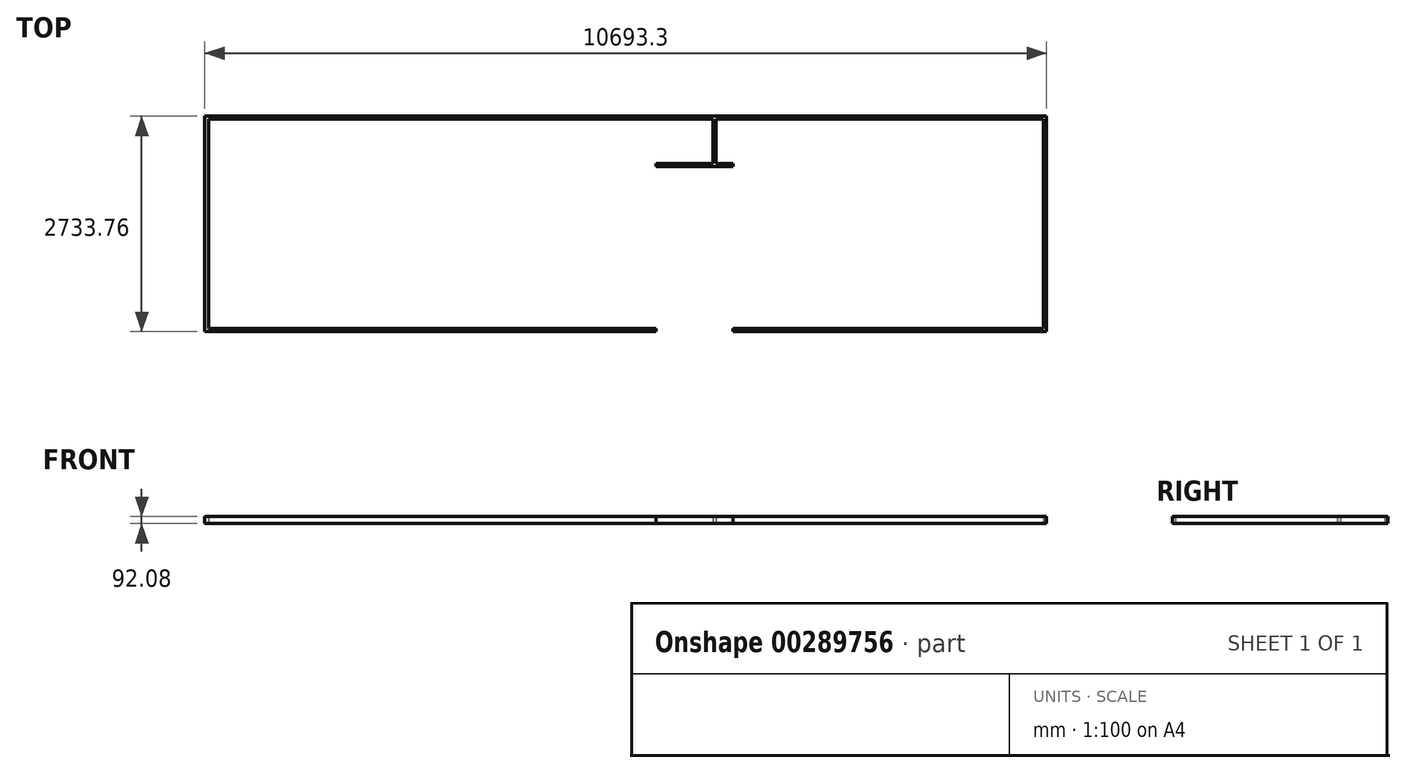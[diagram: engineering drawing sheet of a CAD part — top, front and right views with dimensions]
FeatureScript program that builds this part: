
annotation { "Feature Type Name" : "Feature", "Feature Type Description" : "" }
export const myFeature = defineFeature(function(context is Context, id is Id, definition is map)
    precondition{}
    {
        {
            var Q0;
            Q0=qCreatedBy(makeId("Top.planeOp"),FACE);
            var sketch = newSketch(context, id + "F0", { "sketchPlane" : qUnion([Q0])});
            skLineSegment(sketch, "E0.bottom", {"start": v(5346.65, -1366.88) * mm, "end": v(-5346.65, -1366.88) * mm});
            skLineSegment(sketch, "E0.top", {"start": v(5346.65, 1366.88) * mm, "end": v(-5346.65, 1366.88) * mm});
            skLineSegment(sketch, "E0.left", {"start": v(5346.65, -1366.88) * mm, "end": v(5346.65, 1366.88) * mm});
            skLineSegment(sketch, "E0.right", {"start": v(-5346.65, -1366.88) * mm, "end": v(-5346.65, 1366.88) * mm});
            skPoint(sketch, "E0.middle", {"position": v(0, 0) * mm});
            skLineSegment(sketch, "E1.bottom", {"start": v(-5300.93, 1328.78) * mm, "end": v(5308.55, 1328.78) * mm});
            skLineSegment(sketch, "E1.top", {"start": v(-5300.93, -1328.78) * mm, "end": v(5308.55, -1328.78) * mm});
            skLineSegment(sketch, "E1.left", {"start": v(-5300.93, 1328.78) * mm, "end": v(-5300.93, -1328.78) * mm});
            skLineSegment(sketch, "E1.right", {"start": v(5308.55, 1328.78) * mm, "end": v(5308.55, -1328.78) * mm});
            skLineSegment(sketch, "E2", {"start": v(0, -1328.78) * mm, "end": v(0, 1328.78) * mm, "construction": true});
            skLineSegment(sketch, "E3.bottom", {"start": v(387.25, 1328.78) * mm, "end": v(1365.15, 1328.78) * mm});
            skLineSegment(sketch, "E3.top", {"start": v(387.25, -1328.78) * mm, "end": v(1365.15, -1328.78) * mm});
            skLineSegment(sketch, "E3.left", {"start": v(387.25, 1328.78) * mm, "end": v(387.25, -1328.78) * mm});
            skLineSegment(sketch, "E3.right", {"start": v(1365.15, 1328.78) * mm, "end": v(1365.15, -1328.78) * mm});
            skLineSegment(sketch, "E4.bottom", {"start": v(387.25, 728.62) * mm, "end": v(1365.15, 728.62) * mm});
            skLineSegment(sketch, "E4.top", {"start": v(387.25, 766.72) * mm, "end": v(1365.15, 766.72) * mm});
            skLineSegment(sketch, "E4.left", {"start": v(387.25, 728.62) * mm, "end": v(387.25, 766.72) * mm});
            skLineSegment(sketch, "E4.right", {"start": v(1365.15, 728.62) * mm, "end": v(1365.15, 766.72) * mm});
            skLineSegment(sketch, "E5", {"start": v(349.15, 1328.78) * mm, "end": v(349.15, -1328.78) * mm});
            skLineSegment(sketch, "E6", {"start": v(1403.25, 1328.78) * mm, "end": v(1403.25, -1328.78) * mm});
            skLineSegment(sketch, "E7", {"start": v(876.2, 766.72) * mm, "end": v(876.2, 1328.78) * mm, "construction": true});
            skLineSegment(sketch, "E8.bottom", {"start": v(857, 1328.78) * mm, "end": v(895.4, 1328.78) * mm});
            skLineSegment(sketch, "E8.top", {"start": v(857, 766.72) * mm, "end": v(895.4, 766.72) * mm});
            skLineSegment(sketch, "E8.left", {"start": v(857, 1328.78) * mm, "end": v(857, 766.72) * mm});
            skLineSegment(sketch, "E8.right", {"start": v(895.4, 1328.78) * mm, "end": v(895.4, 766.72) * mm});
            skLineSegment(sketch, "E9.bottom", {"start": v(603.1, 1328.78) * mm, "end": v(641.2, 1328.78) * mm});
            skLineSegment(sketch, "E9.top", {"start": v(603.1, 766.72) * mm, "end": v(641.2, 766.72) * mm});
            skLineSegment(sketch, "E9.left", {"start": v(603.1, 1328.78) * mm, "end": v(603.1, 766.72) * mm});
            skLineSegment(sketch, "E9.right", {"start": v(641.2, 1328.78) * mm, "end": v(641.2, 766.72) * mm});
            skLineSegment(sketch, "E10", {"start": v(622.15, 1328.78) * mm, "end": v(622.15, 766.72) * mm, "construction": true});
            skLineSegment(sketch, "E11.MirrorCS", {"start": v(1111.2, 1328.78) * mm, "end": v(1111.2, 766.72) * mm});
            skLineSegment(sketch, "E12.MirrorCS", {"start": v(1149.3, 1328.78) * mm, "end": v(1149.3, 766.72) * mm});
            skLineSegment(sketch, "E13.bottom", {"start": v(4905.3, 1328.78) * mm, "end": v(4943.4, 1328.78) * mm});
            skLineSegment(sketch, "E13.top", {"start": v(4905.3, -1328.78) * mm, "end": v(4943.4, -1328.78) * mm});
            skLineSegment(sketch, "E13.left", {"start": v(4905.3, 1328.78) * mm, "end": v(4905.3, -1328.78) * mm});
            skLineSegment(sketch, "E13.right", {"start": v(4943.4, 1328.78) * mm, "end": v(4943.4, -1328.78) * mm});
            skLineSegment(sketch, "E14.bottom", {"start": v(4499, 1328.78) * mm, "end": v(4537.1, 1328.78) * mm});
            skLineSegment(sketch, "E14.top", {"start": v(4499, -1328.78) * mm, "end": v(4537.1, -1328.78) * mm});
            skLineSegment(sketch, "E14.left", {"start": v(4499, 1328.78) * mm, "end": v(4499, -1328.78) * mm});
            skLineSegment(sketch, "E14.right", {"start": v(4537.1, 1328.78) * mm, "end": v(4537.1, -1328.78) * mm});
            skLineSegment(sketch, "E15.bottom", {"start": v(4092.7, 1328.78) * mm, "end": v(4130.8, 1328.78) * mm});
            skLineSegment(sketch, "E15.top", {"start": v(4092.7, -1328.78) * mm, "end": v(4130.8, -1328.78) * mm});
            skLineSegment(sketch, "E15.left", {"start": v(4092.7, 1328.78) * mm, "end": v(4092.7, -1328.78) * mm});
            skLineSegment(sketch, "E15.right", {"start": v(4130.8, 1328.78) * mm, "end": v(4130.8, -1328.78) * mm});
            skLineSegment(sketch, "E16.bottom", {"start": v(3686.4, 1328.78) * mm, "end": v(3724.5, 1328.78) * mm});
            skLineSegment(sketch, "E16.top", {"start": v(3686.4, -1328.78) * mm, "end": v(3724.5, -1328.78) * mm});
            skLineSegment(sketch, "E16.left", {"start": v(3686.4, 1328.78) * mm, "end": v(3686.4, -1328.78) * mm});
            skLineSegment(sketch, "E16.right", {"start": v(3724.5, 1328.78) * mm, "end": v(3724.5, -1328.78) * mm});
            skLineSegment(sketch, "E17.bottom", {"start": v(3280.1, 1328.78) * mm, "end": v(3318.2, 1328.78) * mm});
            skLineSegment(sketch, "E17.top", {"start": v(3280.1, -1328.78) * mm, "end": v(3318.2, -1328.78) * mm});
            skLineSegment(sketch, "E17.left", {"start": v(3280.1, 1328.78) * mm, "end": v(3280.1, -1328.78) * mm});
            skLineSegment(sketch, "E17.right", {"start": v(3318.2, 1328.78) * mm, "end": v(3318.2, -1328.78) * mm});
            skLineSegment(sketch, "E18.bottom", {"start": v(2873.8, 1328.78) * mm, "end": v(2911.9, 1328.78) * mm});
            skLineSegment(sketch, "E18.top", {"start": v(2873.8, -1328.78) * mm, "end": v(2911.9, -1328.78) * mm});
            skLineSegment(sketch, "E18.left", {"start": v(2873.8, 1328.78) * mm, "end": v(2873.8, -1328.78) * mm});
            skLineSegment(sketch, "E18.right", {"start": v(2911.9, 1328.78) * mm, "end": v(2911.9, -1328.78) * mm});
            skLineSegment(sketch, "E19.bottom", {"start": v(2467.5, 1328.78) * mm, "end": v(2505.6, 1328.78) * mm});
            skLineSegment(sketch, "E19.top", {"start": v(2467.5, -1328.78) * mm, "end": v(2505.6, -1328.78) * mm});
            skLineSegment(sketch, "E19.left", {"start": v(2467.5, 1328.78) * mm, "end": v(2467.5, -1328.78) * mm});
            skLineSegment(sketch, "E19.right", {"start": v(2505.6, 1328.78) * mm, "end": v(2505.6, -1328.78) * mm});
            skLineSegment(sketch, "E20.bottom", {"start": v(2061.21, 1328.78) * mm, "end": v(2099.31, 1328.78) * mm});
            skLineSegment(sketch, "E20.top", {"start": v(2061.21, -1328.78) * mm, "end": v(2099.31, -1328.78) * mm});
            skLineSegment(sketch, "E20.left", {"start": v(2061.21, 1328.78) * mm, "end": v(2061.21, -1328.78) * mm});
            skLineSegment(sketch, "E20.right", {"start": v(2099.31, 1328.78) * mm, "end": v(2099.31, -1328.78) * mm});
            skLineSegment(sketch, "E21.bottom", {"start": v(1654.91, 1328.78) * mm, "end": v(1693.01, 1328.78) * mm});
            skLineSegment(sketch, "E21.top", {"start": v(1654.91, -1328.78) * mm, "end": v(1693.01, -1328.78) * mm});
            skLineSegment(sketch, "E21.left", {"start": v(1654.91, 1328.78) * mm, "end": v(1654.91, -1328.78) * mm});
            skLineSegment(sketch, "E21.right", {"start": v(1693.01, 1328.78) * mm, "end": v(1693.01, -1328.78) * mm});
            skLineSegment(sketch, "E22.bottom", {"start": v(-4932.73, 1328.78) * mm, "end": v(-4894.63, 1328.78) * mm});
            skLineSegment(sketch, "E22.top", {"start": v(-4932.73, -1328.78) * mm, "end": v(-4894.63, -1328.78) * mm});
            skLineSegment(sketch, "E22.left", {"start": v(-4932.73, 1328.78) * mm, "end": v(-4932.73, -1328.78) * mm});
            skLineSegment(sketch, "E22.right", {"start": v(-4894.63, 1328.78) * mm, "end": v(-4894.63, -1328.78) * mm});
            skLineSegment(sketch, "E23.bottom", {"start": v(-4526.43, 1328.78) * mm, "end": v(-4488.33, 1328.78) * mm});
            skLineSegment(sketch, "E23.top", {"start": v(-4526.43, -1328.78) * mm, "end": v(-4488.33, -1328.78) * mm});
            skLineSegment(sketch, "E23.left", {"start": v(-4526.43, 1328.78) * mm, "end": v(-4526.43, -1328.78) * mm});
            skLineSegment(sketch, "E23.right", {"start": v(-4488.33, 1328.78) * mm, "end": v(-4488.33, -1328.78) * mm});
            skLineSegment(sketch, "E24.bottom", {"start": v(-4120.13, 1328.78) * mm, "end": v(-4082.03, 1328.78) * mm});
            skLineSegment(sketch, "E24.top", {"start": v(-4120.13, -1328.78) * mm, "end": v(-4082.03, -1328.78) * mm});
            skLineSegment(sketch, "E24.left", {"start": v(-4120.13, 1328.78) * mm, "end": v(-4120.13, -1328.78) * mm});
            skLineSegment(sketch, "E24.right", {"start": v(-4082.03, 1328.78) * mm, "end": v(-4082.03, -1328.78) * mm});
            skLineSegment(sketch, "E25.bottom", {"start": v(-3713.84, 1328.78) * mm, "end": v(-3675.74, 1328.78) * mm});
            skLineSegment(sketch, "E25.top", {"start": v(-3713.84, -1328.78) * mm, "end": v(-3675.74, -1328.78) * mm});
            skLineSegment(sketch, "E25.left", {"start": v(-3713.84, 1328.78) * mm, "end": v(-3713.84, -1328.78) * mm});
            skLineSegment(sketch, "E25.right", {"start": v(-3675.74, 1328.78) * mm, "end": v(-3675.74, -1328.78) * mm});
            skLineSegment(sketch, "E26.bottom", {"start": v(-3307.54, 1328.78) * mm, "end": v(-3269.44, 1328.78) * mm});
            skLineSegment(sketch, "E26.top", {"start": v(-3307.54, -1328.78) * mm, "end": v(-3269.44, -1328.78) * mm});
            skLineSegment(sketch, "E26.left", {"start": v(-3307.54, 1328.78) * mm, "end": v(-3307.54, -1328.78) * mm});
            skLineSegment(sketch, "E26.right", {"start": v(-3269.44, 1328.78) * mm, "end": v(-3269.44, -1328.78) * mm});
            skLineSegment(sketch, "E27.bottom", {"start": v(-2901.24, 1328.78) * mm, "end": v(-2863.14, 1328.78) * mm});
            skLineSegment(sketch, "E27.top", {"start": v(-2901.24, -1328.78) * mm, "end": v(-2863.14, -1328.78) * mm});
            skLineSegment(sketch, "E27.left", {"start": v(-2901.24, 1328.78) * mm, "end": v(-2901.24, -1328.78) * mm});
            skLineSegment(sketch, "E27.right", {"start": v(-2863.14, 1328.78) * mm, "end": v(-2863.14, -1328.78) * mm});
            skLineSegment(sketch, "E28.bottom", {"start": v(-2494.94, 1328.78) * mm, "end": v(-2456.84, 1328.78) * mm});
            skLineSegment(sketch, "E28.top", {"start": v(-2494.94, -1328.78) * mm, "end": v(-2456.84, -1328.78) * mm});
            skLineSegment(sketch, "E28.left", {"start": v(-2494.94, 1328.78) * mm, "end": v(-2494.94, -1328.78) * mm});
            skLineSegment(sketch, "E28.right", {"start": v(-2456.84, 1328.78) * mm, "end": v(-2456.84, -1328.78) * mm});
            skLineSegment(sketch, "E29.bottom", {"start": v(-2088.64, 1328.78) * mm, "end": v(-2050.54, 1328.78) * mm});
            skLineSegment(sketch, "E29.top", {"start": v(-2088.64, -1328.78) * mm, "end": v(-2050.54, -1328.78) * mm});
            skLineSegment(sketch, "E29.left", {"start": v(-2088.64, 1328.78) * mm, "end": v(-2088.64, -1328.78) * mm});
            skLineSegment(sketch, "E29.right", {"start": v(-2050.54, 1328.78) * mm, "end": v(-2050.54, -1328.78) * mm});
            skLineSegment(sketch, "E30.bottom", {"start": v(-1682.34, 1328.78) * mm, "end": v(-1644.24, 1328.78) * mm});
            skLineSegment(sketch, "E30.top", {"start": v(-1682.34, -1328.78) * mm, "end": v(-1644.24, -1328.78) * mm});
            skLineSegment(sketch, "E30.left", {"start": v(-1682.34, 1328.78) * mm, "end": v(-1682.34, -1328.78) * mm});
            skLineSegment(sketch, "E30.right", {"start": v(-1644.24, 1328.78) * mm, "end": v(-1644.24, -1328.78) * mm});
            skLineSegment(sketch, "E31.bottom", {"start": v(-1276.05, 1328.78) * mm, "end": v(-1237.95, 1328.78) * mm});
            skLineSegment(sketch, "E31.top", {"start": v(-1276.05, -1328.78) * mm, "end": v(-1237.95, -1328.78) * mm});
            skLineSegment(sketch, "E31.left", {"start": v(-1276.05, 1328.78) * mm, "end": v(-1276.05, -1328.78) * mm});
            skLineSegment(sketch, "E31.right", {"start": v(-1237.95, 1328.78) * mm, "end": v(-1237.95, -1328.78) * mm});
            skLineSegment(sketch, "E32.bottom", {"start": v(-869.75, 1328.78) * mm, "end": v(-831.65, 1328.78) * mm});
            skLineSegment(sketch, "E32.top", {"start": v(-869.75, -1328.78) * mm, "end": v(-831.65, -1328.78) * mm});
            skLineSegment(sketch, "E32.left", {"start": v(-869.75, 1328.78) * mm, "end": v(-869.75, -1328.78) * mm});
            skLineSegment(sketch, "E32.right", {"start": v(-831.65, 1328.78) * mm, "end": v(-831.65, -1328.78) * mm});
            skLineSegment(sketch, "E33.bottom", {"start": v(-463.45, 1328.78) * mm, "end": v(-425.35, 1328.78) * mm});
            skLineSegment(sketch, "E33.top", {"start": v(-463.45, -1328.78) * mm, "end": v(-425.35, -1328.78) * mm});
            skLineSegment(sketch, "E33.left", {"start": v(-463.45, 1328.78) * mm, "end": v(-463.45, -1328.78) * mm});
            skLineSegment(sketch, "E33.right", {"start": v(-425.35, 1328.78) * mm, "end": v(-425.35, -1328.78) * mm});
            skLineSegment(sketch, "E34.bottom", {"start": v(-57.15, 1328.78) * mm, "end": v(-19.05, 1328.78) * mm});
            skLineSegment(sketch, "E34.top", {"start": v(-57.15, -1328.78) * mm, "end": v(-19.05, -1328.78) * mm});
            skLineSegment(sketch, "E34.left", {"start": v(-57.15, 1328.78) * mm, "end": v(-57.15, -1328.78) * mm});
            skLineSegment(sketch, "E34.right", {"start": v(-19.05, 1328.78) * mm, "end": v(-19.05, -1328.78) * mm});
            skLineSegment(sketch, "E35", {"start": v(1365.15, -1328.78) * mm, "end": v(1365.15, -1366.88) * mm});
            skLineSegment(sketch, "E36", {"start": v(387.25, -1328.78) * mm, "end": v(387.25, -1366.88) * mm});
            skSolve(sketch);
        }
        {
            var Q0;
            {var subQ0=sQuery(id+"F0.wireOp",EDGE,"e03bbd14-4e46-43d8-a5f9-80b2dea7db7f0.MirrorCS");Q0=makeQuery(id+"F0.imprint","IMPRINT",FACE,{"disambiguationData":[TD([[makeQuery(id+"F0.imprint","IMPRINT",EDGE,{"derivedFrom":subQ0}),1.0]])]});}
            var Q1;
            {var subQ7=sQuery(id+"F0.wireOp",EDGE,"EFqx7HEP-Nfe9-0ldO-Yoev-NmYAcbnf758y");Q1=makeQuery(id+"F0.imprint","IMPRINT",FACE,{"disambiguationData":[TD([[makeQuery(id+"F0.imprint","IMPRINT",EDGE,{"derivedFrom":subQ7}),-1.0]])]});}
            var Q2;
            {var subQ0=sQuery(id+"F0.wireOp",EDGE,"edbdd21b-7951-4497-ac7e-6e46abb4ccd70.MirrorCS");Q2=makeQuery(id+"F0.imprint","IMPRINT",FACE,{"disambiguationData":[TD([[makeQuery(id+"F0.imprint","IMPRINT",EDGE,{"derivedFrom":subQ0}),-1.0]])]});}
            var Q3;
            {var subQ0=sQuery(id+"F0.wireOp",EDGE,"7de17b8e-8469-475a-b975-fd82b060c23f0.MirrorCS");Q3=makeQuery(id+"F0.imprint","IMPRINT",FACE,{"disambiguationData":[TD([[makeQuery(id+"F0.imprint","IMPRINT",EDGE,{"derivedFrom":subQ0}),1.0]])]});}
            var Q4;
            {var subQ5=sQuery(id+"F0.wireOp",EDGE,"4AthFqkJ-wqFj-7w0H-RTdV-ZVLi3eRejgEJ.bottom");var subQ8=sQuery(id+"F0.wireOp",EDGE,"8f4d6e74-220d-450d-a5c4-15dd5d45fac50.MirrorCS");var subQ10=makeQuery(id+"F0.imprint","INTERSECT",VERTEX,{"derivedFrom":[subQ5,subQ8]});Q4=makeQuery(id+"F0.imprint","IMPRINT",FACE,{"disambiguationData":[TD([[makeQuery(id+"F0.imprint","IMPRINT",EDGE,{"disambiguationData":[TD([[subQ10,-1.0]])],"derivedFrom":subQ5}),1.0]])]});}
            var Q5;
            {var subQ0=sQuery(id+"F0.wireOp",EDGE,"b7a96eb8-1ea0-4e2f-8a00-b5aa0dec934b0.MirrorCS");Q5=makeQuery(id+"F0.imprint","IMPRINT",FACE,{"disambiguationData":[TD([[makeQuery(id+"F0.imprint","IMPRINT",EDGE,{"derivedFrom":subQ0}),-1.0]])]});}
            var Q6;
            {var subQ0=sQuery(id+"F0.wireOp",EDGE,"da11186a-d0f2-4cc5-8c91-6d18c19f1f220.MirrorCS");Q6=makeQuery(id+"F0.imprint","IMPRINT",FACE,{"disambiguationData":[TD([[makeQuery(id+"F0.imprint","IMPRINT",EDGE,{"derivedFrom":subQ0}),-1.0]])]});}
            var Q7;
            {var subQ0=sQuery(id+"F0.wireOp",EDGE,"f72f8c2a-f3f3-459a-8ec0-e048655b896d0.MirrorCS");var subQ1=sQuery(id+"F0.wireOp",EDGE,"4AthFqkJ-wqFj-7w0H-RTdV-ZVLi3eRejgEJ.top");var subQ2=makeQuery(id+"F0.imprint","INTERSECT",VERTEX,{"derivedFrom":[subQ1,subQ0]});Q7=makeQuery(id+"F0.imprint","IMPRINT",FACE,{"disambiguationData":[TD([[makeQuery(id+"F0.imprint","IMPRINT",EDGE,{"disambiguationData":[TD([[subQ2,-1.0]])],"derivedFrom":subQ1}),1.0]])]});}
            var Q8;
            {var subQ5=sQuery(id+"F0.wireOp",EDGE,"eca8af08-4f88-4f9e-b7fb-055b73c8b4f30.MirrorCS");var subQ7=sQuery(id+"F0.wireOp",EDGE,"4AthFqkJ-wqFj-7w0H-RTdV-ZVLi3eRejgEJ.bottom");var subQ8=makeQuery(id+"F0.imprint","INTERSECT",VERTEX,{"derivedFrom":[subQ7,subQ5]});Q8=makeQuery(id+"F0.imprint","IMPRINT",FACE,{"disambiguationData":[TD([[makeQuery(id+"F0.imprint","IMPRINT",EDGE,{"disambiguationData":[TD([[subQ8,-1.0]])],"derivedFrom":subQ7}),1.0]])]});}
            var Q9;
            {var subQ4=sQuery(id+"F0.wireOp",EDGE,"6c1e8db1-4096-4c37-9079-9901a149bb3d0.MirrorCS");var subQ7=sQuery(id+"F0.wireOp",EDGE,"4AthFqkJ-wqFj-7w0H-RTdV-ZVLi3eRejgEJ.bottom");var subQ10=makeQuery(id+"F0.imprint","INTERSECT",VERTEX,{"derivedFrom":[subQ7,subQ4]});Q9=makeQuery(id+"F0.imprint","IMPRINT",FACE,{"disambiguationData":[TD([[makeQuery(id+"F0.imprint","IMPRINT",EDGE,{"disambiguationData":[TD([[subQ10,-1.0]])],"derivedFrom":subQ7}),1.0]])]});}
            var Q10;
            {var subQ0=sQuery(id+"F0.wireOp",EDGE,"55050aa2-543b-4654-a200-01c89433912e0.MirrorCS");var subQ1=sQuery(id+"F0.wireOp",EDGE,"4AthFqkJ-wqFj-7w0H-RTdV-ZVLi3eRejgEJ.top");var subQ2=makeQuery(id+"F0.imprint","INTERSECT",VERTEX,{"derivedFrom":[subQ1,subQ0]});Q10=makeQuery(id+"F0.imprint","IMPRINT",FACE,{"disambiguationData":[TD([[makeQuery(id+"F0.imprint","IMPRINT",EDGE,{"disambiguationData":[TD([[subQ2,1.0]])],"derivedFrom":subQ1}),1.0]])]});}
            var Q11;
            {var subQ3=sQuery(id+"F0.wireOp",EDGE,"3aWXcNN2-d2y1-1F6M-5Hkd-EHZ6NJIHuSP8");Q11=makeQuery(id+"F0.imprint","IMPRINT",FACE,{"disambiguationData":[TD([[makeQuery(id+"F0.imprint","IMPRINT",EDGE,{"derivedFrom":subQ3}),-1.0]])]});}
            var Q12;
            {var subQ6=sQuery(id+"F0.wireOp",EDGE,"4AthFqkJ-wqFj-7w0H-RTdV-ZVLi3eRejgEJ.left");Q12=makeQuery(id+"F0.imprint","IMPRINT",FACE,{"disambiguationData":[TD([[makeQuery(id+"F0.imprint","IMPRINT",EDGE,{"derivedFrom":subQ6}),-1.0]])]});}
            var Q13;
            {var subQ0=sQuery(id+"F0.wireOp",EDGE,"92030646-e98a-4083-b465-eda06a02aa580.MirrorCS");Q13=makeQuery(id+"F0.imprint","IMPRINT",FACE,{"disambiguationData":[TD([[makeQuery(id+"F0.imprint","IMPRINT",EDGE,{"derivedFrom":subQ0}),1.0]])]});}
            var Q14;
            {var subQ0=sQuery(id+"F0.wireOp",EDGE,"0e344b7f-dcc7-4a3f-8939-196222c3ee7a0.MirrorCS");Q14=makeQuery(id+"F0.imprint","IMPRINT",FACE,{"disambiguationData":[TD([[makeQuery(id+"F0.imprint","IMPRINT",EDGE,{"derivedFrom":subQ0}),-1.0]])]});}
            var Q15;
            {var subQ0=sQuery(id+"F0.wireOp",EDGE,"95ca570f-170f-43a6-b84c-d3a65055c82b0.MirrorCS");Q15=makeQuery(id+"F0.imprint","IMPRINT",FACE,{"disambiguationData":[TD([[makeQuery(id+"F0.imprint","IMPRINT",EDGE,{"derivedFrom":subQ0}),1.0]])]});}
            var Q16;
            {var subQ4=sQuery(id+"F0.wireOp",EDGE,"8a681850-bd4a-4ca6-8d45-30870cc5114b0.MirrorCS");var subQ5=sQuery(id+"F0.wireOp",EDGE,"4AthFqkJ-wqFj-7w0H-RTdV-ZVLi3eRejgEJ.bottom");var subQ6=makeQuery(id+"F0.imprint","INTERSECT",VERTEX,{"derivedFrom":[subQ5,subQ4]});Q16=makeQuery(id+"F0.imprint","IMPRINT",FACE,{"disambiguationData":[TD([[makeQuery(id+"F0.imprint","IMPRINT",EDGE,{"disambiguationData":[TD([[subQ6,-1.0]])],"derivedFrom":subQ5}),1.0]])]});}
            var Q17;
            {var subQ4=sQuery(id+"F0.wireOp",EDGE,"4AthFqkJ-wqFj-7w0H-RTdV-ZVLi3eRejgEJ.bottom");var subQ8=sQuery(id+"F0.wireOp",EDGE,"5ed274ad-43b9-4acb-bec6-48bd2bb972420.MirrorCS");var subQ10=makeQuery(id+"F0.imprint","INTERSECT",VERTEX,{"derivedFrom":[subQ4,subQ8]});Q17=makeQuery(id+"F0.imprint","IMPRINT",FACE,{"disambiguationData":[TD([[makeQuery(id+"F0.imprint","IMPRINT",EDGE,{"disambiguationData":[TD([[subQ10,-1.0]])],"derivedFrom":subQ4}),1.0]])]});}
            var Q18;
            {var subQ5=sQuery(id+"F0.wireOp",EDGE,"bf3aad54-d5d8-4dbd-ba34-4691da0b365d0.MirrorCS");var subQ7=sQuery(id+"F0.wireOp",EDGE,"4AthFqkJ-wqFj-7w0H-RTdV-ZVLi3eRejgEJ.bottom");var subQ8=makeQuery(id+"F0.imprint","INTERSECT",VERTEX,{"derivedFrom":[subQ7,subQ5]});Q18=makeQuery(id+"F0.imprint","IMPRINT",FACE,{"disambiguationData":[TD([[makeQuery(id+"F0.imprint","IMPRINT",EDGE,{"disambiguationData":[TD([[subQ8,-1.0]])],"derivedFrom":subQ7}),1.0]])]});}
            var Q19;
            {var subQ0=sQuery(id+"F0.wireOp",EDGE,"7ad01133-0a83-40c2-aee9-f517a01396690.MirrorCS");var subQ1=sQuery(id+"F0.wireOp",EDGE,"4AthFqkJ-wqFj-7w0H-RTdV-ZVLi3eRejgEJ.top");var subQ2=makeQuery(id+"F0.imprint","INTERSECT",VERTEX,{"derivedFrom":[subQ1,subQ0]});Q19=makeQuery(id+"F0.imprint","IMPRINT",FACE,{"disambiguationData":[TD([[makeQuery(id+"F0.imprint","IMPRINT",EDGE,{"disambiguationData":[TD([[subQ2,1.0]])],"derivedFrom":subQ1}),1.0]])]});}
            var Q20;
            {var subQ3=sQuery(id+"F0.wireOp",EDGE,"0632b321-56e7-4b31-9cd1-585e07a893ff0.MirrorCS");var subQ4=sQuery(id+"F0.wireOp",EDGE,"4AthFqkJ-wqFj-7w0H-RTdV-ZVLi3eRejgEJ.bottom");var subQ5=makeQuery(id+"F0.imprint","INTERSECT",VERTEX,{"derivedFrom":[subQ4,subQ3]});Q20=makeQuery(id+"F0.imprint","IMPRINT",FACE,{"disambiguationData":[TD([[makeQuery(id+"F0.imprint","IMPRINT",EDGE,{"disambiguationData":[TD([[subQ5,-1.0]])],"derivedFrom":subQ4}),1.0]])]});}
            var Q21;
            {var subQ4=sQuery(id+"F0.wireOp",EDGE,"4AthFqkJ-wqFj-7w0H-RTdV-ZVLi3eRejgEJ.bottom");var subQ8=sQuery(id+"F0.wireOp",EDGE,"1bcce820-757c-45ce-a4fe-54bff22ba8310.MirrorCS");var subQ10=makeQuery(id+"F0.imprint","INTERSECT",VERTEX,{"derivedFrom":[subQ4,subQ8]});Q21=makeQuery(id+"F0.imprint","IMPRINT",FACE,{"disambiguationData":[TD([[makeQuery(id+"F0.imprint","IMPRINT",EDGE,{"disambiguationData":[TD([[subQ10,-1.0]])],"derivedFrom":subQ4}),1.0]])]});}
            var Q22;
            {var subQ8=sQuery(id+"F0.wireOp",EDGE,"4AthFqkJ-wqFj-7w0H-RTdV-ZVLi3eRejgEJ.right");Q22=makeQuery(id+"F0.imprint","IMPRINT",FACE,{"disambiguationData":[TD([[makeQuery(id+"F0.imprint","IMPRINT",EDGE,{"derivedFrom":subQ8}),1.0]])]});}
            var Q23;
            {var subQ0=sQuery(id+"F0.wireOp",EDGE,"1b9fc814-7275-47f6-8dd0-aeae657b9ac90.MirrorCS");var subQ1=sQuery(id+"F0.wireOp",EDGE,"4AthFqkJ-wqFj-7w0H-RTdV-ZVLi3eRejgEJ.top");var subQ2=makeQuery(id+"F0.imprint","INTERSECT",VERTEX,{"derivedFrom":[subQ1,subQ0]});Q23=makeQuery(id+"F0.imprint","IMPRINT",FACE,{"disambiguationData":[TD([[makeQuery(id+"F0.imprint","IMPRINT",EDGE,{"disambiguationData":[TD([[subQ2,-1.0]])],"derivedFrom":subQ1}),1.0]])]});}
            var Q24;
            {var subQ0=sQuery(id+"F0.wireOp",EDGE,"0493b29f-ec4a-4c4c-ac9e-8fdb3be76d310.MirrorCS");Q24=makeQuery(id+"F0.imprint","IMPRINT",FACE,{"disambiguationData":[TD([[makeQuery(id+"F0.imprint","IMPRINT",EDGE,{"derivedFrom":subQ0}),1.0]])]});}
            var Q25;
            {var subQ0=sQuery(id+"F0.wireOp",EDGE,"63c733ed-a5aa-43e7-ab23-9ab8c604324c0.MirrorCS");Q25=makeQuery(id+"F0.imprint","IMPRINT",FACE,{"disambiguationData":[TD([[makeQuery(id+"F0.imprint","IMPRINT",EDGE,{"derivedFrom":subQ0}),1.0]])]});}
            var Q26;
            {var subQ5=sQuery(id+"F0.wireOp",EDGE,"E6GgMG58-NzDt-iqJW-TLqZ-AtfXyUXh4wKe");Q26=makeQuery(id+"F0.imprint","IMPRINT",FACE,{"disambiguationData":[TD([[makeQuery(id+"F0.imprint","IMPRINT",EDGE,{"derivedFrom":subQ5}),1.0]])]});}
            var Q27;
            {var subQ6=sQuery(id+"F0.wireOp",EDGE,"3aWXcNN2-d2y1-1F6M-5Hkd-EHZ6NJIHuSP8");Q27=makeQuery(id+"F0.imprint","IMPRINT",FACE,{"disambiguationData":[TD([[makeQuery(id+"F0.imprint","IMPRINT",EDGE,{"derivedFrom":subQ6}),1.0]])]});}
            var Q28;
            {var subQ6=sQuery(id+"F0.wireOp",EDGE,"E6GgMG58-NzDt-iqJW-TLqZ-AtfXyUXh4wKe");Q28=makeQuery(id+"F0.imprint","IMPRINT",FACE,{"disambiguationData":[TD([[makeQuery(id+"F0.imprint","IMPRINT",EDGE,{"derivedFrom":subQ6}),-1.0]])]});}
            var Q29;
            {var subQ0=sQuery(id+"F0.wireOp",EDGE,"xTM1oSQN-q9p7-LrQJ-wgkP-syFjsQtJfwuK.bottom");Q29=makeQuery(id+"F0.imprint","IMPRINT",FACE,{"disambiguationData":[TD([[makeQuery(id+"F0.imprint","IMPRINT",EDGE,{"derivedFrom":subQ0}),-1.0]])]});}
            var Q30;
            {var subQ0=sQuery(id+"F0.wireOp",EDGE,"xTM1oSQN-q9p7-LrQJ-wgkP-syFjsQtJfwuK.top");Q30=makeQuery(id+"F0.imprint","IMPRINT",FACE,{"disambiguationData":[TD([[makeQuery(id+"F0.imprint","IMPRINT",EDGE,{"derivedFrom":subQ0}),1.0]])]});}
            var Q31;
            {var subQ1=sQuery(id+"F0.wireOp",EDGE,"xTM1oSQN-q9p7-LrQJ-wgkP-syFjsQtJfwuK.bottom");Q31=makeQuery(id+"F0.imprint","IMPRINT",FACE,{"disambiguationData":[TD([[makeQuery(id+"F0.imprint","IMPRINT",EDGE,{"derivedFrom":subQ1}),1.0]])]});}
            var Q32;
            Q32=makeQuery(id+"F0.imprint","IMPRINT",FACE,{"disambiguationData":[TD([[makeQuery(id+"F0.imprint","IMPRINT",EDGE,{"derivedFrom":sQuery(id+"F0.wireOp",EDGE,"w7in2STq-dmfq-Ztst-uc13-PS53EKAe34f7.top")}),1.0]])]});
            var Q33;
            {var subQ5=sQuery(id+"F0.wireOp",EDGE,"8ijx6biu-ALKk-pq3C-dhgc-nGGqiL4vIiWN");var subQ7=sQuery(id+"F0.wireOp",EDGE,"8a681850-bd4a-4ca6-8d45-30870cc5114b0.MirrorCS");var subQ8=makeQuery(id+"F0.imprint","INTERSECT",VERTEX,{"derivedFrom":[subQ7,subQ5]});Q33=makeQuery(id+"F0.imprint","IMPRINT",FACE,{"disambiguationData":[TD([[makeQuery(id+"F0.imprint","IMPRINT",EDGE,{"disambiguationData":[TD([[subQ8,1.0]])],"derivedFrom":subQ7}),-1.0]])]});}
            var Q34;
            {var subQ7=sQuery(id+"F0.wireOp",EDGE,"0632b321-56e7-4b31-9cd1-585e07a893ff0.MirrorCS");var subQ9=sQuery(id+"F0.wireOp",EDGE,"8ijx6biu-ALKk-pq3C-dhgc-nGGqiL4vIiWN");var subQ10=makeQuery(id+"F0.imprint","INTERSECT",VERTEX,{"derivedFrom":[subQ7,subQ9]});Q34=makeQuery(id+"F0.imprint","IMPRINT",FACE,{"disambiguationData":[TD([[makeQuery(id+"F0.imprint","IMPRINT",EDGE,{"disambiguationData":[TD([[subQ10,1.0]])],"derivedFrom":subQ7}),-1.0]])]});}
            var Q35;
            {var subQ5=sQuery(id+"F0.wireOp",EDGE,"8ijx6biu-ALKk-pq3C-dhgc-nGGqiL4vIiWN");var subQ6=sQuery(id+"F0.wireOp",EDGE,"019fe33c-2ba7-4981-a1aa-b8912489248e0.MirrorCS");var subQ7=makeQuery(id+"F0.imprint","INTERSECT",VERTEX,{"derivedFrom":[subQ6,subQ5]});Q35=makeQuery(id+"F0.imprint","IMPRINT",FACE,{"disambiguationData":[TD([[makeQuery(id+"F0.imprint","IMPRINT",EDGE,{"disambiguationData":[TD([[subQ7,1.0]])],"derivedFrom":subQ6}),-1.0]])]});}
            var Q36;
            {var subQ4=sQuery(id+"F0.wireOp",EDGE,"8ijx6biu-ALKk-pq3C-dhgc-nGGqiL4vIiWN");var subQ7=sQuery(id+"F0.wireOp",EDGE,"f7381abf-e9df-4e1a-a30e-4fe6b1d368c50.MirrorCS");var subQ8=makeQuery(id+"F0.imprint","INTERSECT",VERTEX,{"derivedFrom":[subQ7,subQ4]});Q36=makeQuery(id+"F0.imprint","IMPRINT",FACE,{"disambiguationData":[TD([[makeQuery(id+"F0.imprint","IMPRINT",EDGE,{"disambiguationData":[TD([[subQ8,1.0]])],"derivedFrom":subQ7}),-1.0]])]});}
            var Q37;
            {var subQ3=sQuery(id+"F0.wireOp",EDGE,"8ijx6biu-ALKk-pq3C-dhgc-nGGqiL4vIiWN");var subQ7=sQuery(id+"F0.wireOp",EDGE,"6c1e8db1-4096-4c37-9079-9901a149bb3d0.MirrorCS");var subQ8=makeQuery(id+"F0.imprint","INTERSECT",VERTEX,{"derivedFrom":[subQ7,subQ3]});Q37=makeQuery(id+"F0.imprint","IMPRINT",FACE,{"disambiguationData":[TD([[makeQuery(id+"F0.imprint","IMPRINT",EDGE,{"disambiguationData":[TD([[subQ8,1.0]])],"derivedFrom":subQ7}),-1.0]])]});}
            var Q38;
            {var subQ4=sQuery(id+"F0.wireOp",EDGE,"8ijx6biu-ALKk-pq3C-dhgc-nGGqiL4vIiWN");var subQ7=sQuery(id+"F0.wireOp",EDGE,"8f4d6e74-220d-450d-a5c4-15dd5d45fac50.MirrorCS");var subQ8=makeQuery(id+"F0.imprint","INTERSECT",VERTEX,{"derivedFrom":[subQ7,subQ4]});Q38=makeQuery(id+"F0.imprint","IMPRINT",FACE,{"disambiguationData":[TD([[makeQuery(id+"F0.imprint","IMPRINT",EDGE,{"disambiguationData":[TD([[subQ8,1.0]])],"derivedFrom":subQ7}),-1.0]])]});}
            var Q39;
            {var subQ0=sQuery(id+"F0.wireOp",EDGE,"KcFaNi3p-Mqzx-hNtU-70nu-rjvwtTVn4XIA");Q39=makeQuery(id+"F0.imprint","IMPRINT",FACE,{"disambiguationData":[TD([[makeQuery(id+"F0.imprint","IMPRINT",EDGE,{"derivedFrom":subQ0}),-1.0]])]});}
            var Q40;
            {var subQ7=sQuery(id+"F0.wireOp",EDGE,"JvJ4ZzyL-X5yR-yT1t-gWen-LnuBgDK7jZsF");Q40=makeQuery(id+"F0.imprint","IMPRINT",FACE,{"disambiguationData":[TD([[makeQuery(id+"F0.imprint","IMPRINT",EDGE,{"derivedFrom":subQ7}),1.0]])]});}
            var Q41;
            {var subQ5=sQuery(id+"F0.wireOp",EDGE,"8ijx6biu-ALKk-pq3C-dhgc-nGGqiL4vIiWN");var subQ6=sQuery(id+"F0.wireOp",EDGE,"bf3aad54-d5d8-4dbd-ba34-4691da0b365d0.MirrorCS");var subQ7=makeQuery(id+"F0.imprint","INTERSECT",VERTEX,{"derivedFrom":[subQ6,subQ5]});Q41=makeQuery(id+"F0.imprint","IMPRINT",FACE,{"disambiguationData":[TD([[makeQuery(id+"F0.imprint","IMPRINT",EDGE,{"disambiguationData":[TD([[subQ7,1.0]])],"derivedFrom":subQ6}),-1.0]])]});}
            var Q42;
            {var subQ5=sQuery(id+"F0.wireOp",EDGE,"8ijx6biu-ALKk-pq3C-dhgc-nGGqiL4vIiWN");var subQ7=sQuery(id+"F0.wireOp",EDGE,"5ed274ad-43b9-4acb-bec6-48bd2bb972420.MirrorCS");var subQ8=makeQuery(id+"F0.imprint","INTERSECT",VERTEX,{"derivedFrom":[subQ7,subQ5]});Q42=makeQuery(id+"F0.imprint","IMPRINT",FACE,{"disambiguationData":[TD([[makeQuery(id+"F0.imprint","IMPRINT",EDGE,{"disambiguationData":[TD([[subQ8,1.0]])],"derivedFrom":subQ7}),-1.0]])]});}
            var Q43;
            {var subQ0=sQuery(id+"F0.wireOp",EDGE,"EFqx7HEP-Nfe9-0ldO-Yoev-NmYAcbnf758y");Q43=makeQuery(id+"F0.imprint","IMPRINT",FACE,{"disambiguationData":[TD([[makeQuery(id+"F0.imprint","IMPRINT",EDGE,{"derivedFrom":subQ0}),1.0]])]});}
            var Q44;
            {var subQ0=sQuery(id+"F0.wireOp",EDGE,"QlbIkJlA-GZXo-uyBw-HzbM-woG2F7svoY3c");Q44=makeQuery(id+"F0.imprint","IMPRINT",FACE,{"disambiguationData":[TD([[makeQuery(id+"F0.imprint","IMPRINT",EDGE,{"derivedFrom":subQ0}),1.0]])]});}
            var Q45;
            {var subQ0=sQuery(id+"F0.wireOp",EDGE,"iGA4u3sP-0zRX-MU7R-LLKM-kgWDpWtacOll");Q45=makeQuery(id+"F0.imprint","IMPRINT",FACE,{"disambiguationData":[TD([[makeQuery(id+"F0.imprint","IMPRINT",EDGE,{"derivedFrom":subQ0}),-1.0]])]});}
            var Q46;
            {var subQ0=sQuery(id+"F0.wireOp",EDGE,"iGA4u3sP-0zRX-MU7R-LLKM-kgWDpWtacOll");Q46=makeQuery(id+"F0.imprint","IMPRINT",FACE,{"disambiguationData":[TD([[makeQuery(id+"F0.imprint","IMPRINT",EDGE,{"derivedFrom":subQ0}),1.0]])]});}
            var Q47;
            {var subQ0=sQuery(id+"F0.wireOp",EDGE,"t5sFcsg7-FEeG-W394-4G1u-bvZyn1PHE7l8");Q47=makeQuery(id+"F0.imprint","IMPRINT",FACE,{"disambiguationData":[TD([[makeQuery(id+"F0.imprint","IMPRINT",EDGE,{"derivedFrom":subQ0}),-1.0]])]});}
            var Q48;
            {var subQ0=sQuery(id+"F0.wireOp",EDGE,"gSGAxQI9-OKXq-k85j-osUc-OuGH0ZGV6Hf7");var subQ1=sQuery(id+"F0.wireOp",EDGE,"c3f41723-229c-4d74-ac07-4786d7f9cf2e0.MirrorCS");var subQ2=makeQuery(id+"F0.imprint","INTERSECT",VERTEX,{"derivedFrom":[subQ1,subQ0]});Q48=makeQuery(id+"F0.imprint","IMPRINT",FACE,{"disambiguationData":[TD([[makeQuery(id+"F0.imprint","IMPRINT",EDGE,{"disambiguationData":[TD([[subQ2,-1.0]])],"derivedFrom":subQ1}),1.0]])]});}
            var Q49;
            {var subQ0=sQuery(id+"F0.wireOp",EDGE,"gSGAxQI9-OKXq-k85j-osUc-OuGH0ZGV6Hf7");var subQ1=sQuery(id+"F0.wireOp",EDGE,"c3f41723-229c-4d74-ac07-4786d7f9cf2e0.MirrorCS");var subQ2=makeQuery(id+"F0.imprint","INTERSECT",VERTEX,{"derivedFrom":[subQ1,subQ0]});Q49=makeQuery(id+"F0.imprint","IMPRINT",FACE,{"disambiguationData":[TD([[makeQuery(id+"F0.imprint","IMPRINT",EDGE,{"disambiguationData":[TD([[subQ2,-1.0]])],"derivedFrom":subQ1}),-1.0]])]});}
            var Q50;
            {var subQ0=sQuery(id+"F0.wireOp",EDGE,"gSGAxQI9-OKXq-k85j-osUc-OuGH0ZGV6Hf7");var subQ1=sQuery(id+"F0.wireOp",EDGE,"5f963c61-5f66-4834-8852-3989dfd0aaaa0.MirrorCS");var subQ2=makeQuery(id+"F0.imprint","INTERSECT",VERTEX,{"derivedFrom":[subQ1,subQ0]});Q50=makeQuery(id+"F0.imprint","IMPRINT",FACE,{"disambiguationData":[TD([[makeQuery(id+"F0.imprint","IMPRINT",EDGE,{"disambiguationData":[TD([[subQ2,-1.0]])],"derivedFrom":subQ1}),1.0]])]});}
            var Q51;
            {var subQ0=sQuery(id+"F0.wireOp",EDGE,"br4IC8WJ-HBUO-pzxn-8otQ-qS1CwRbFTHxP");Q51=makeQuery(id+"F0.imprint","IMPRINT",FACE,{"disambiguationData":[TD([[makeQuery(id+"F0.imprint","IMPRINT",EDGE,{"derivedFrom":subQ0}),1.0]])]});}
            var Q52;
            {var subQ0=sQuery(id+"F0.wireOp",EDGE,"gSGAxQI9-OKXq-k85j-osUc-OuGH0ZGV6Hf7");var subQ1=sQuery(id+"F0.wireOp",EDGE,"8106601b-d97d-4dcf-b6dc-423d0e0e66910.MirrorCS");var subQ2=makeQuery(id+"F0.imprint","INTERSECT",VERTEX,{"derivedFrom":[subQ1,subQ0]});Q52=makeQuery(id+"F0.imprint","IMPRINT",FACE,{"disambiguationData":[TD([[makeQuery(id+"F0.imprint","IMPRINT",EDGE,{"disambiguationData":[TD([[subQ2,-1.0]])],"derivedFrom":subQ1}),1.0]])]});}
            var Q53;
            {var subQ0=sQuery(id+"F0.wireOp",EDGE,"KcFaNi3p-Mqzx-hNtU-70nu-rjvwtTVn4XIA");Q53=makeQuery(id+"F0.imprint","IMPRINT",FACE,{"disambiguationData":[TD([[makeQuery(id+"F0.imprint","IMPRINT",EDGE,{"derivedFrom":subQ0}),-1.0]])]});}
            var Q54;
            {var subQ0=sQuery(id+"F0.wireOp",EDGE,"1b9fc814-7275-47f6-8dd0-aeae657b9ac90.MirrorCS");var subQ1=sQuery(id+"F0.wireOp",EDGE,"4AthFqkJ-wqFj-7w0H-RTdV-ZVLi3eRejgEJ.top");var subQ2=makeQuery(id+"F0.imprint","INTERSECT",VERTEX,{"derivedFrom":[subQ1,subQ0]});Q54=makeQuery(id+"F0.imprint","IMPRINT",FACE,{"disambiguationData":[TD([[makeQuery(id+"F0.imprint","IMPRINT",EDGE,{"disambiguationData":[TD([[subQ2,-1.0]])],"derivedFrom":subQ1}),1.0]])]});}
            var Q55;
            {var subQ0=sQuery(id+"F0.wireOp",EDGE,"95ca570f-170f-43a6-b84c-d3a65055c82b0.MirrorCS");Q55=makeQuery(id+"F0.imprint","IMPRINT",FACE,{"disambiguationData":[TD([[makeQuery(id+"F0.imprint","IMPRINT",EDGE,{"derivedFrom":subQ0}),1.0]])]});}
            var Q56;
            {var subQ0=sQuery(id+"F0.wireOp",EDGE,"f72f8c2a-f3f3-459a-8ec0-e048655b896d0.MirrorCS");var subQ1=sQuery(id+"F0.wireOp",EDGE,"4AthFqkJ-wqFj-7w0H-RTdV-ZVLi3eRejgEJ.top");var subQ2=makeQuery(id+"F0.imprint","INTERSECT",VERTEX,{"derivedFrom":[subQ1,subQ0]});Q56=makeQuery(id+"F0.imprint","IMPRINT",FACE,{"disambiguationData":[TD([[makeQuery(id+"F0.imprint","IMPRINT",EDGE,{"disambiguationData":[TD([[subQ2,-1.0]])],"derivedFrom":subQ1}),1.0]])]});}
            var Q57;
            {var subQ0=sQuery(id+"F0.wireOp",EDGE,"92030646-e98a-4083-b465-eda06a02aa580.MirrorCS");Q57=makeQuery(id+"F0.imprint","IMPRINT",FACE,{"disambiguationData":[TD([[makeQuery(id+"F0.imprint","IMPRINT",EDGE,{"derivedFrom":subQ0}),1.0]])]});}
            var Q58;
            {var subQ0=sQuery(id+"F0.wireOp",EDGE,"7ad01133-0a83-40c2-aee9-f517a01396690.MirrorCS");var subQ1=sQuery(id+"F0.wireOp",EDGE,"4AthFqkJ-wqFj-7w0H-RTdV-ZVLi3eRejgEJ.top");var subQ2=makeQuery(id+"F0.imprint","INTERSECT",VERTEX,{"derivedFrom":[subQ1,subQ0]});Q58=makeQuery(id+"F0.imprint","IMPRINT",FACE,{"disambiguationData":[TD([[makeQuery(id+"F0.imprint","IMPRINT",EDGE,{"disambiguationData":[TD([[subQ2,1.0]])],"derivedFrom":subQ1}),1.0]])]});}
            var Q59;
            {var subQ0=sQuery(id+"F0.wireOp",EDGE,"da11186a-d0f2-4cc5-8c91-6d18c19f1f220.MirrorCS");Q59=makeQuery(id+"F0.imprint","IMPRINT",FACE,{"disambiguationData":[TD([[makeQuery(id+"F0.imprint","IMPRINT",EDGE,{"derivedFrom":subQ0}),-1.0]])]});}
            var Q60;
            {var subQ0=sQuery(id+"F0.wireOp",EDGE,"55050aa2-543b-4654-a200-01c89433912e0.MirrorCS");var subQ1=sQuery(id+"F0.wireOp",EDGE,"4AthFqkJ-wqFj-7w0H-RTdV-ZVLi3eRejgEJ.top");var subQ2=makeQuery(id+"F0.imprint","INTERSECT",VERTEX,{"derivedFrom":[subQ1,subQ0]});Q60=makeQuery(id+"F0.imprint","IMPRINT",FACE,{"disambiguationData":[TD([[makeQuery(id+"F0.imprint","IMPRINT",EDGE,{"disambiguationData":[TD([[subQ2,1.0]])],"derivedFrom":subQ1}),1.0]])]});}
            var Q61;
            {var subQ2=sQuery(id+"F0.wireOp",EDGE,"6c1e8db1-4096-4c37-9079-9901a149bb3d0.MirrorCS");var subQ6=sQuery(id+"F0.wireOp",EDGE,"fd0a6f88-e381-4c68-814f-5e4faa0d84f72.MirrorCS");var subQ9=makeQuery(id+"F0.imprint","INTERSECT",VERTEX,{"derivedFrom":[subQ2,subQ6]});Q61=makeQuery(id+"F0.imprint","IMPRINT",FACE,{"disambiguationData":[TD([[makeQuery(id+"F0.imprint","IMPRINT",EDGE,{"disambiguationData":[TD([[subQ9,1.0]])],"derivedFrom":subQ2}),-1.0]])]});}
            var Q62;
            {var subQ2=sQuery(id+"F0.wireOp",EDGE,"f7381abf-e9df-4e1a-a30e-4fe6b1d368c50.MirrorCS");var subQ4=sQuery(id+"F0.wireOp",EDGE,"fd0a6f88-e381-4c68-814f-5e4faa0d84f72.MirrorCS");var subQ9=makeQuery(id+"F0.imprint","INTERSECT",VERTEX,{"derivedFrom":[subQ2,subQ4]});Q62=makeQuery(id+"F0.imprint","IMPRINT",FACE,{"disambiguationData":[TD([[makeQuery(id+"F0.imprint","IMPRINT",EDGE,{"disambiguationData":[TD([[subQ9,1.0]])],"derivedFrom":subQ2}),-1.0]])]});}
            var Q63;
            {var subQ2=sQuery(id+"F0.wireOp",EDGE,"f7381abf-e9df-4e1a-a30e-4fe6b1d368c50.MirrorCS");var subQ7=sQuery(id+"F0.wireOp",EDGE,"fd0a6f88-e381-4c68-814f-5e4faa0d84f72.MirrorCS");var subQ9=makeQuery(id+"F0.imprint","INTERSECT",VERTEX,{"derivedFrom":[subQ2,subQ7]});Q63=makeQuery(id+"F0.imprint","IMPRINT",FACE,{"disambiguationData":[TD([[makeQuery(id+"F0.imprint","IMPRINT",EDGE,{"disambiguationData":[TD([[subQ9,1.0]])],"derivedFrom":subQ2}),1.0]])]});}
            var Q64;
            {var subQ4=sQuery(id+"F0.wireOp",EDGE,"fd0a6f88-e381-4c68-814f-5e4faa0d84f72.MirrorCS");var subQ11=sQuery(id+"F0.wireOp",EDGE,"8a681850-bd4a-4ca6-8d45-30870cc5114b0.MirrorCS");var subQ12=makeQuery(id+"F0.imprint","INTERSECT",VERTEX,{"derivedFrom":[subQ11,subQ4]});Q64=makeQuery(id+"F0.imprint","IMPRINT",FACE,{"disambiguationData":[TD([[makeQuery(id+"F0.imprint","IMPRINT",EDGE,{"disambiguationData":[TD([[subQ12,1.0]])],"derivedFrom":subQ11}),-1.0]])]});}
            var Q65;
            {var subQ3=sQuery(id+"F0.wireOp",EDGE,"eca8af08-4f88-4f9e-b7fb-055b73c8b4f30.MirrorCS");var subQ5=sQuery(id+"F0.wireOp",EDGE,"fd0a6f88-e381-4c68-814f-5e4faa0d84f72.MirrorCS");var subQ9=makeQuery(id+"F0.imprint","INTERSECT",VERTEX,{"derivedFrom":[subQ3,subQ5]});Q65=makeQuery(id+"F0.imprint","IMPRINT",FACE,{"disambiguationData":[TD([[makeQuery(id+"F0.imprint","IMPRINT",EDGE,{"disambiguationData":[TD([[subQ9,1.0]])],"derivedFrom":subQ3}),-1.0]])]});}
            var Q66;
            {var subQ2=sQuery(id+"F0.wireOp",EDGE,"1bcce820-757c-45ce-a4fe-54bff22ba8310.MirrorCS");var subQ4=sQuery(id+"F0.wireOp",EDGE,"fd0a6f88-e381-4c68-814f-5e4faa0d84f72.MirrorCS");var subQ5=makeQuery(id+"F0.imprint","INTERSECT",VERTEX,{"derivedFrom":[subQ2,subQ4]});Q66=makeQuery(id+"F0.imprint","IMPRINT",FACE,{"disambiguationData":[TD([[makeQuery(id+"F0.imprint","IMPRINT",EDGE,{"disambiguationData":[TD([[subQ5,1.0]])],"derivedFrom":subQ2}),-1.0]])]});}
            var Q67;
            {var subQ0=sQuery(id+"F0.wireOp",EDGE,"w7in2STq-dmfq-Ztst-uc13-PS53EKAe34f7.left");Q67=makeQuery(id+"F0.imprint","IMPRINT",FACE,{"disambiguationData":[TD([[makeQuery(id+"F0.imprint","IMPRINT",EDGE,{"derivedFrom":subQ0}),1.0]])]});}
            var Q68;
            {var subQ0=sQuery(id+"F0.wireOp",EDGE,"fd0a6f88-e381-4c68-814f-5e4faa0d84f70.MirrorCS");var subQ1=sQuery(id+"F0.wireOp",EDGE,"xTM1oSQN-q9p7-LrQJ-wgkP-syFjsQtJfwuK.left");var subQ2=makeQuery(id+"F0.imprint","INTERSECT",VERTEX,{"derivedFrom":[subQ1,subQ0]});Q68=makeQuery(id+"F0.imprint","IMPRINT",FACE,{"disambiguationData":[TD([[makeQuery(id+"F0.imprint","IMPRINT",EDGE,{"disambiguationData":[TD([[subQ2,1.0]])],"derivedFrom":subQ1}),1.0]])]});}
            var Q69;
            {var subQ0=sQuery(id+"F0.wireOp",EDGE,"fd0a6f88-e381-4c68-814f-5e4faa0d84f70.MirrorCS");var subQ1=sQuery(id+"F0.wireOp",EDGE,"573c87d8-b675-496e-a079-9395e3357b8d0.MirrorCS");var subQ2=makeQuery(id+"F0.imprint","INTERSECT",VERTEX,{"derivedFrom":[subQ1,subQ0]});Q69=makeQuery(id+"F0.imprint","IMPRINT",FACE,{"disambiguationData":[TD([[makeQuery(id+"F0.imprint","IMPRINT",EDGE,{"disambiguationData":[TD([[subQ2,1.0]])],"derivedFrom":subQ1}),1.0]])]});}
            var Q70;
            {var subQ5=sQuery(id+"F0.wireOp",EDGE,"fd0a6f88-e381-4c68-814f-5e4faa0d84f76.MirrorCS");var subQ7=sQuery(id+"F0.wireOp",EDGE,"1bcce820-757c-45ce-a4fe-54bff22ba8310.MirrorCS");var subQ8=makeQuery(id+"F0.imprint","INTERSECT",VERTEX,{"derivedFrom":[subQ7,subQ5]});Q70=makeQuery(id+"F0.imprint","IMPRINT",FACE,{"disambiguationData":[TD([[makeQuery(id+"F0.imprint","IMPRINT",EDGE,{"disambiguationData":[TD([[subQ8,-1.0]])],"derivedFrom":subQ7}),-1.0]])]});}
            var Q71;
            {var subQ3=sQuery(id+"F0.wireOp",EDGE,"fd0a6f88-e381-4c68-814f-5e4faa0d84f76.MirrorCS");var subQ4=sQuery(id+"F0.wireOp",EDGE,"eca8af08-4f88-4f9e-b7fb-055b73c8b4f30.MirrorCS");var subQ5=makeQuery(id+"F0.imprint","INTERSECT",VERTEX,{"derivedFrom":[subQ4,subQ3]});Q71=makeQuery(id+"F0.imprint","IMPRINT",FACE,{"disambiguationData":[TD([[makeQuery(id+"F0.imprint","IMPRINT",EDGE,{"disambiguationData":[TD([[subQ5,-1.0]])],"derivedFrom":subQ4}),-1.0]])]});}
            var Q72;
            {var subQ0=sQuery(id+"F0.wireOp",EDGE,"fd0a6f88-e381-4c68-814f-5e4faa0d84f70.MirrorCS");var subQ1=sQuery(id+"F0.wireOp",EDGE,"9fe0fe99-07bc-4679-9664-f55d6f2dc43d0.MirrorCS");var subQ2=makeQuery(id+"F0.imprint","INTERSECT",VERTEX,{"derivedFrom":[subQ1,subQ0]});Q72=makeQuery(id+"F0.imprint","IMPRINT",FACE,{"disambiguationData":[TD([[makeQuery(id+"F0.imprint","IMPRINT",EDGE,{"disambiguationData":[TD([[subQ2,1.0]])],"derivedFrom":subQ1}),1.0]])]});}
            var Q73;
            {var subQ2=sQuery(id+"F0.wireOp",EDGE,"8a681850-bd4a-4ca6-8d45-30870cc5114b0.MirrorCS");var subQ4=sQuery(id+"F0.wireOp",EDGE,"fd0a6f88-e381-4c68-814f-5e4faa0d84f76.MirrorCS");var subQ5=makeQuery(id+"F0.imprint","INTERSECT",VERTEX,{"derivedFrom":[subQ2,subQ4]});Q73=makeQuery(id+"F0.imprint","IMPRINT",FACE,{"disambiguationData":[TD([[makeQuery(id+"F0.imprint","IMPRINT",EDGE,{"disambiguationData":[TD([[subQ5,-1.0]])],"derivedFrom":subQ2}),-1.0]])]});}
            var Q74;
            {var subQ0=sQuery(id+"F0.wireOp",EDGE,"fd0a6f88-e381-4c68-814f-5e4faa0d84f70.MirrorCS");var subQ1=sQuery(id+"F0.wireOp",EDGE,"1b0e9755-274d-47f2-9ad2-c5868fe4f0aa0.MirrorCS");var subQ2=makeQuery(id+"F0.imprint","INTERSECT",VERTEX,{"derivedFrom":[subQ1,subQ0]});Q74=makeQuery(id+"F0.imprint","IMPRINT",FACE,{"disambiguationData":[TD([[makeQuery(id+"F0.imprint","IMPRINT",EDGE,{"disambiguationData":[TD([[subQ2,1.0]])],"derivedFrom":subQ1}),1.0]])]});}
            var Q75;
            {var subQ0=sQuery(id+"F0.wireOp",EDGE,"fd0a6f88-e381-4c68-814f-5e4faa0d84f73.MirrorCS");var subQ1=sQuery(id+"F0.wireOp",EDGE,"fd0a6f88-e381-4c68-814f-5e4faa0d84f70.MirrorCS");var subQ2=makeQuery(id+"F0.imprint","INTERSECT",VERTEX,{"derivedFrom":[subQ1,subQ0]});Q75=makeQuery(id+"F0.imprint","IMPRINT",FACE,{"disambiguationData":[TD([[makeQuery(id+"F0.imprint","IMPRINT",EDGE,{"disambiguationData":[TD([[subQ2,1.0]])],"derivedFrom":subQ1}),-1.0]])]});}
            var Q76;
            {var subQ0=sQuery(id+"F0.wireOp",EDGE,"fd0a6f88-e381-4c68-814f-5e4faa0d84f77.MirrorCS");Q76=makeQuery(id+"F0.imprint","IMPRINT",FACE,{"disambiguationData":[TD([[makeQuery(id+"F0.imprint","IMPRINT",EDGE,{"derivedFrom":subQ0}),1.0]])]});}
            var Q77;
            {var subQ5=sQuery(id+"F0.wireOp",EDGE,"YzBnu5k0-fbgq-BqNp-rjJW-YDCBdr94ePzX");Q77=makeQuery(id+"F0.imprint","IMPRINT",FACE,{"disambiguationData":[TD([[makeQuery(id+"F0.imprint","IMPRINT",EDGE,{"derivedFrom":subQ5}),-1.0]])]});}
            var Q78;
            {var subQ0=sQuery(id+"F0.wireOp",EDGE,"fd0a6f88-e381-4c68-814f-5e4faa0d84f70.MirrorCS");var subQ1=sQuery(id+"F0.wireOp",EDGE,"SCgSlVHH-Jo2y-DwYx-939J-i8zndRqhXNfp");var subQ2=makeQuery(id+"F0.imprint","INTERSECT",VERTEX,{"derivedFrom":[subQ1,subQ0]});Q78=makeQuery(id+"F0.imprint","IMPRINT",FACE,{"disambiguationData":[TD([[makeQuery(id+"F0.imprint","IMPRINT",EDGE,{"disambiguationData":[TD([[subQ2,1.0]])],"derivedFrom":subQ1}),1.0]])]});}
            var Q79;
            {var subQ5=sQuery(id+"F0.wireOp",EDGE,"fd0a6f88-e381-4c68-814f-5e4faa0d84f76.MirrorCS");var subQ8=sQuery(id+"F0.wireOp",EDGE,"6c1e8db1-4096-4c37-9079-9901a149bb3d0.MirrorCS");var subQ10=makeQuery(id+"F0.imprint","INTERSECT",VERTEX,{"derivedFrom":[subQ8,subQ5]});Q79=makeQuery(id+"F0.imprint","IMPRINT",FACE,{"disambiguationData":[TD([[makeQuery(id+"F0.imprint","IMPRINT",EDGE,{"disambiguationData":[TD([[subQ10,-1.0]])],"derivedFrom":subQ8}),-1.0]])]});}
            var Q80;
            {var subQ0=sQuery(id+"F0.wireOp",EDGE,"fd0a6f88-e381-4c68-814f-5e4faa0d84f70.MirrorCS");var subQ1=sQuery(id+"F0.wireOp",EDGE,"2c59450c-3f31-460a-8c07-403c14a947670.MirrorCS");var subQ2=makeQuery(id+"F0.imprint","INTERSECT",VERTEX,{"derivedFrom":[subQ1,subQ0]});Q80=makeQuery(id+"F0.imprint","IMPRINT",FACE,{"disambiguationData":[TD([[makeQuery(id+"F0.imprint","IMPRINT",EDGE,{"disambiguationData":[TD([[subQ2,1.0]])],"derivedFrom":subQ1}),1.0]])]});}
            var Q81;
            Q81=makeQuery(id+"F0.imprint","IMPRINT",FACE,{"disambiguationData":[TD([[makeQuery(id+"F0.imprint","IMPRINT",EDGE,{"derivedFrom":sQuery(id+"F0.wireOp",EDGE,"E0.bottom")}),-1.0]])]});
            var Q82;
            Q82=makeQuery(id+"F0.imprint","IMPRINT",FACE,{"disambiguationData":[TD([[makeQuery(id+"F0.imprint","IMPRINT",EDGE,{"derivedFrom":sQuery(id+"F0.wireOp",EDGE,"E22.bottom")}),-1.0]])]});
            var Q83;
            Q83=makeQuery(id+"F0.imprint","IMPRINT",FACE,{"disambiguationData":[TD([[makeQuery(id+"F0.imprint","IMPRINT",EDGE,{"derivedFrom":sQuery(id+"F0.wireOp",EDGE,"E23.bottom")}),-1.0]])]});
            var Q84;
            Q84=makeQuery(id+"F0.imprint","IMPRINT",FACE,{"disambiguationData":[TD([[makeQuery(id+"F0.imprint","IMPRINT",EDGE,{"derivedFrom":sQuery(id+"F0.wireOp",EDGE,"E24.bottom")}),-1.0]])]});
            var Q85;
            Q85=makeQuery(id+"F0.imprint","IMPRINT",FACE,{"disambiguationData":[TD([[makeQuery(id+"F0.imprint","IMPRINT",EDGE,{"derivedFrom":sQuery(id+"F0.wireOp",EDGE,"E25.bottom")}),-1.0]])]});
            var Q86;
            Q86=makeQuery(id+"F0.imprint","IMPRINT",FACE,{"disambiguationData":[TD([[makeQuery(id+"F0.imprint","IMPRINT",EDGE,{"derivedFrom":sQuery(id+"F0.wireOp",EDGE,"E26.bottom")}),-1.0]])]});
            var Q87;
            Q87=makeQuery(id+"F0.imprint","IMPRINT",FACE,{"disambiguationData":[TD([[makeQuery(id+"F0.imprint","IMPRINT",EDGE,{"derivedFrom":sQuery(id+"F0.wireOp",EDGE,"E27.bottom")}),-1.0]])]});
            var Q88;
            Q88=makeQuery(id+"F0.imprint","IMPRINT",FACE,{"disambiguationData":[TD([[makeQuery(id+"F0.imprint","IMPRINT",EDGE,{"derivedFrom":sQuery(id+"F0.wireOp",EDGE,"E28.bottom")}),-1.0]])]});
            var Q89;
            Q89=makeQuery(id+"F0.imprint","IMPRINT",FACE,{"disambiguationData":[TD([[makeQuery(id+"F0.imprint","IMPRINT",EDGE,{"derivedFrom":sQuery(id+"F0.wireOp",EDGE,"E29.bottom")}),-1.0]])]});
            var Q90;
            Q90=makeQuery(id+"F0.imprint","IMPRINT",FACE,{"disambiguationData":[TD([[makeQuery(id+"F0.imprint","IMPRINT",EDGE,{"derivedFrom":sQuery(id+"F0.wireOp",EDGE,"E30.bottom")}),-1.0]])]});
            var Q91;
            Q91=makeQuery(id+"F0.imprint","IMPRINT",FACE,{"disambiguationData":[TD([[makeQuery(id+"F0.imprint","IMPRINT",EDGE,{"derivedFrom":sQuery(id+"F0.wireOp",EDGE,"E31.bottom")}),-1.0]])]});
            var Q92;
            Q92=makeQuery(id+"F0.imprint","IMPRINT",FACE,{"disambiguationData":[TD([[makeQuery(id+"F0.imprint","IMPRINT",EDGE,{"derivedFrom":sQuery(id+"F0.wireOp",EDGE,"E32.bottom")}),-1.0]])]});
            var Q93;
            Q93=makeQuery(id+"F0.imprint","IMPRINT",FACE,{"disambiguationData":[TD([[makeQuery(id+"F0.imprint","IMPRINT",EDGE,{"derivedFrom":sQuery(id+"F0.wireOp",EDGE,"E33.bottom")}),-1.0]])]});
            var Q94;
            {var subQ3=sQuery(id+"F0.wireOp",EDGE,"E4.left");Q94=makeQuery(id+"F0.imprint","IMPRINT",FACE,{"disambiguationData":[TD([[makeQuery(id+"F0.imprint","IMPRINT",EDGE,{"derivedFrom":subQ3}),1.0]])]});}
            var Q95;
            Q95=makeQuery(id+"F0.imprint","IMPRINT",FACE,{"disambiguationData":[TD([[makeQuery(id+"F0.imprint","IMPRINT",EDGE,{"derivedFrom":sQuery(id+"F0.wireOp",EDGE,"E4.bottom")}),1.0]])]});
            var Q96;
            Q96=makeQuery(id+"F0.imprint","IMPRINT",FACE,{"disambiguationData":[TD([[makeQuery(id+"F0.imprint","IMPRINT",EDGE,{"derivedFrom":sQuery(id+"F0.wireOp",EDGE,"E9.bottom")}),-1.0]])]});
            var Q97;
            Q97=makeQuery(id+"F0.imprint","IMPRINT",FACE,{"disambiguationData":[TD([[makeQuery(id+"F0.imprint","IMPRINT",EDGE,{"derivedFrom":sQuery(id+"F0.wireOp",EDGE,"E8.bottom")}),-1.0]])]});
            var Q98;
            {var subQ0=sQuery(id+"F0.wireOp",EDGE,"E11.MirrorCS");Q98=makeQuery(id+"F0.imprint","IMPRINT",FACE,{"disambiguationData":[TD([[makeQuery(id+"F0.imprint","IMPRINT",EDGE,{"derivedFrom":subQ0}),1.0]])]});}
            var Q99;
            {var subQ3=sQuery(id+"F0.wireOp",EDGE,"E4.right");Q99=makeQuery(id+"F0.imprint","IMPRINT",FACE,{"disambiguationData":[TD([[makeQuery(id+"F0.imprint","IMPRINT",EDGE,{"derivedFrom":subQ3}),-1.0]])]});}
            var Q100;
            Q100=makeQuery(id+"F0.imprint","IMPRINT",FACE,{"disambiguationData":[TD([[makeQuery(id+"F0.imprint","IMPRINT",EDGE,{"derivedFrom":sQuery(id+"F0.wireOp",EDGE,"E21.bottom")}),-1.0]])]});
            var Q101;
            Q101=makeQuery(id+"F0.imprint","IMPRINT",FACE,{"disambiguationData":[TD([[makeQuery(id+"F0.imprint","IMPRINT",EDGE,{"derivedFrom":sQuery(id+"F0.wireOp",EDGE,"E20.bottom")}),-1.0]])]});
            var Q102;
            Q102=makeQuery(id+"F0.imprint","IMPRINT",FACE,{"disambiguationData":[TD([[makeQuery(id+"F0.imprint","IMPRINT",EDGE,{"derivedFrom":sQuery(id+"F0.wireOp",EDGE,"E19.bottom")}),-1.0]])]});
            var Q103;
            Q103=makeQuery(id+"F0.imprint","IMPRINT",FACE,{"disambiguationData":[TD([[makeQuery(id+"F0.imprint","IMPRINT",EDGE,{"derivedFrom":sQuery(id+"F0.wireOp",EDGE,"E18.bottom")}),-1.0]])]});
            var Q104;
            Q104=makeQuery(id+"F0.imprint","IMPRINT",FACE,{"disambiguationData":[TD([[makeQuery(id+"F0.imprint","IMPRINT",EDGE,{"derivedFrom":sQuery(id+"F0.wireOp",EDGE,"E17.bottom")}),-1.0]])]});
            var Q105;
            Q105=makeQuery(id+"F0.imprint","IMPRINT",FACE,{"disambiguationData":[TD([[makeQuery(id+"F0.imprint","IMPRINT",EDGE,{"derivedFrom":sQuery(id+"F0.wireOp",EDGE,"E16.bottom")}),-1.0]])]});
            var Q106;
            Q106=makeQuery(id+"F0.imprint","IMPRINT",FACE,{"disambiguationData":[TD([[makeQuery(id+"F0.imprint","IMPRINT",EDGE,{"derivedFrom":sQuery(id+"F0.wireOp",EDGE,"E15.bottom")}),-1.0]])]});
            var Q107;
            Q107=makeQuery(id+"F0.imprint","IMPRINT",FACE,{"disambiguationData":[TD([[makeQuery(id+"F0.imprint","IMPRINT",EDGE,{"derivedFrom":sQuery(id+"F0.wireOp",EDGE,"E14.bottom")}),-1.0]])]});
            var Q108;
            Q108=makeQuery(id+"F0.imprint","IMPRINT",FACE,{"disambiguationData":[TD([[makeQuery(id+"F0.imprint","IMPRINT",EDGE,{"derivedFrom":sQuery(id+"F0.wireOp",EDGE,"E13.bottom")}),-1.0]])]});
            var Q109;
            Q109=makeQuery(id+"F0.imprint","IMPRINT",FACE,{"disambiguationData":[TD([[makeQuery(id+"F0.imprint","IMPRINT",EDGE,{"derivedFrom":sQuery(id+"F0.wireOp",EDGE,"E34.bottom")}),-1.0]])]});
            extrude(context, id + "F1", {"entities" : qUnion([Q0, Q1, Q2, Q3, Q4, Q5, Q6, Q7, Q8, Q9, Q10, Q11, Q12, Q13, Q14, Q15, Q16, Q17, Q18, Q19, Q20, Q21, Q22, Q23, Q24, Q25, Q26, Q27, Q28, Q29, Q30, Q31, Q32, Q33, Q34, Q35, Q36, Q37, Q38, Q39, Q40, Q41, Q42, Q43, Q44, Q45, Q46, Q47, Q48, Q49, Q50, Q51, Q52, Q53, Q54, Q55, Q56, Q57, Q58, Q59, Q60, Q61, Q62, Q63, Q64, Q65, Q66, Q67, Q68, Q69, Q70, Q71, Q72, Q73, Q74, Q75, Q76, Q77, Q78, Q79, Q80, Q81, Q82, Q83, Q84, Q85, Q86, Q87, Q88, Q89, Q90, Q91, Q92, Q93, Q94, Q95, Q96, Q97, Q98, Q99, Q100, Q101, Q102, Q103, Q104, Q105, Q106, Q107, Q108, Q109]), "offsetDistance" : 30.48 * mm, "depth" : 92.08 * mm});
        }
    });
